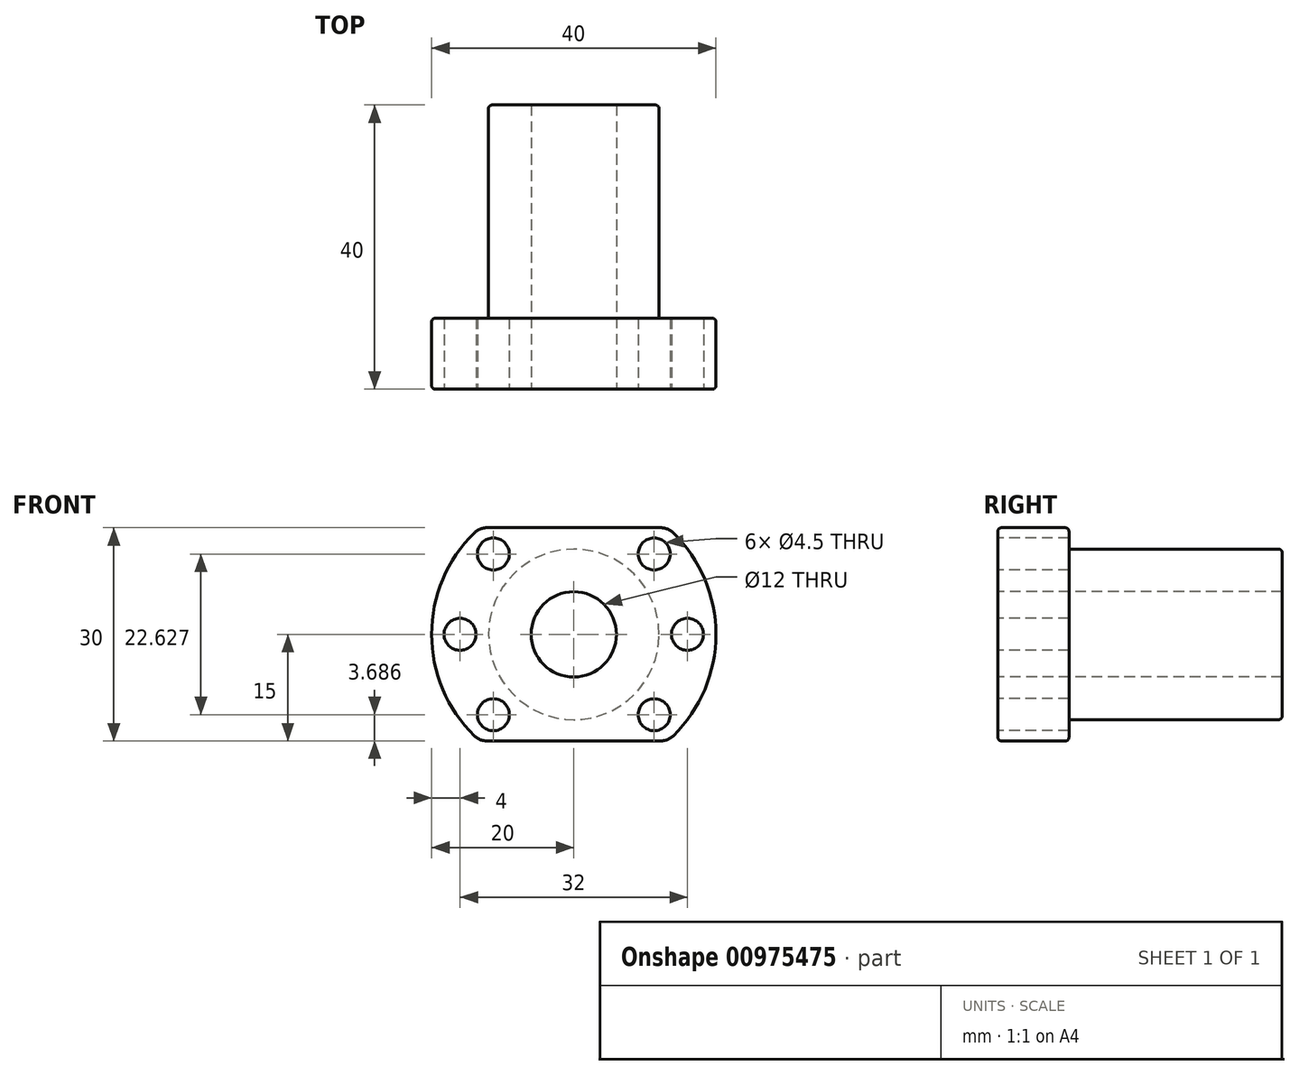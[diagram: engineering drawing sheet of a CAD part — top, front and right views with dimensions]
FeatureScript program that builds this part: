
annotation { "Feature Type Name" : "Feature", "Feature Type Description" : "" }
export const myFeature = defineFeature(function(context is Context, id is Id, definition is map)
    precondition{}
    {
        {
            var Q0;
            Q0=qCreatedBy(makeId("Front.planeOp"),FACE);
            var sketch = newSketch(context, id + "F0", { "sketchPlane" : qUnion([Q0])});
            skCircle(sketch, "E0", {"center": v(0, 0) * mm, "radius": 6 * mm});
            skSolve(sketch);
        }
        {
            var Q0;
            Q0=qCreatedBy(makeId("Front.planeOp"),FACE);
            var sketch = newSketch(context, id + "F1", { "sketchPlane" : qUnion([Q0])});
            skCircle(sketch, "E1.0", {"center": v(0, 0) * mm, "radius": 6 * mm});
            skArc(sketch, "E2", {"start": v(-13.23, 15) * mm, "mid": v(-20, 0) * mm, "end": v(-13.23, -15) * mm});
            skCircle(sketch, "E3", {"center": v(0, 0) * mm, "radius": 12 * mm});
            skLineSegment(sketch, "E4.bottom", {"start": v(-13.23, 15) * mm, "end": v(13.23, 15) * mm});
            skLineSegment(sketch, "E4.top", {"start": v(-13.23, -15) * mm, "end": v(13.23, -15) * mm});
            skArc(sketch, "E5.trimOffspring", {"start": v(13.23, -15) * mm, "mid": v(20, 0) * mm, "end": v(13.23, 15) * mm});
            skCircle(sketch, "E6", {"center": v(0, 0) * mm, "radius": 16 * mm, "construction": true});
            skCircle(sketch, "E7", {"center": v(16, 0) * mm, "radius": 2.25 * mm});
            skCircle(sketch, "E8", {"center": v(11.31, 11.31) * mm, "radius": 2.25 * mm});
            skLineSegment(sketch, "E9", {"start": v(0, 0) * mm, "end": v(11.31, 11.31) * mm, "construction": true});
            skLineSegment(sketch, "E10", {"start": v(0, 0) * mm, "end": v(16, 0) * mm, "construction": true});
            skCircle(sketch, "E11.MirrorC", {"center": v(11.31, -11.31) * mm, "radius": 2.25 * mm});
            skCircle(sketch, "E12.MirrorC", {"center": v(-11.31, 11.31) * mm, "radius": 2.25 * mm});
            skCircle(sketch, "E13.MirrorC", {"center": v(-16, 0) * mm, "radius": 2.25 * mm});
            skCircle(sketch, "E14.MirrorC", {"center": v(-11.31, -11.31) * mm, "radius": 2.25 * mm});
            skSolve(sketch);
        }
        {
            var Q0;
            Q0=makeQuery(id+"F1.imprint","IMPRINT",FACE,{"disambiguationData":[TD([[makeQuery(id+"F1.imprint","IMPRINT",EDGE,{"derivedFrom":sQuery(id+"F1.wireOp",EDGE,"E1.0")}),-1.0]])]});
            extrude(context, id + "F2", {"entities" : qUnion([Q0]), "oppositeDirection" : true, "offsetDistance" : 25 * mm, "depth" : 40 * mm});
        }
        {
            var Q0;
            Q0=makeQuery(id+"F1.imprint","IMPRINT",FACE,{"disambiguationData":[TD([[makeQuery(id+"F1.imprint","IMPRINT",EDGE,{"derivedFrom":sQuery(id+"F1.wireOp",EDGE,"E3")}),-1.0]])]});
            extrude(context, id + "F3", {"entities" : qUnion([Q0]), "operationType" : NewBodyOperationType.ADD, "oppositeDirection" : true, "offsetDistance" : 25 * mm, "depth" : 10 * mm});
        }
        {
            var Q0;
            {var subQ0=sQuery(id+"F1.wireOp",EDGE,"E2");var subQ1=sQuery(id+"F1.wireOp",EDGE,"E4.bottom");Q0=makeQuery(id+"F3.opExtrude","SWEPT_EDGE",EDGE,{"disambiguationData":[OSD([subQ0,subQ1]),TDD([makeQuery(id+"F1.imprint","INTERSECT",VERTEX,{"disambiguationData":[OD(1.0)],"derivedFrom":[subQ0,subQ1]})])]});}
            var Q1;
            {var subQ0=sQuery(id+"F1.wireOp",EDGE,"E2");var subQ1=sQuery(id+"F1.wireOp",EDGE,"E4.bottom");Q1=makeQuery(id+"F3.opExtrude","SWEPT_EDGE",EDGE,{"disambiguationData":[OSD([subQ0,subQ1]),TDD([makeQuery(id+"F1.imprint","INTERSECT",VERTEX,{"disambiguationData":[OD(0.0)],"derivedFrom":[subQ0,subQ1]})])]});}
            var Q2;
            {var subQ0=sQuery(id+"F1.wireOp",EDGE,"E2");var subQ1=sQuery(id+"F1.wireOp",EDGE,"E4.top");Q2=makeQuery(id+"F3.opExtrude","SWEPT_EDGE",EDGE,{"disambiguationData":[OSD([subQ0,subQ1]),TDD([makeQuery(id+"F1.imprint","INTERSECT",VERTEX,{"disambiguationData":[OD(1.0)],"derivedFrom":[subQ0,subQ1]})])]});}
            var Q3;
            {var subQ0=sQuery(id+"F1.wireOp",EDGE,"E2");var subQ1=sQuery(id+"F1.wireOp",EDGE,"E4.top");Q3=makeQuery(id+"F3.opExtrude","SWEPT_EDGE",EDGE,{"disambiguationData":[OSD([subQ0,subQ1]),TDD([makeQuery(id+"F1.imprint","INTERSECT",VERTEX,{"disambiguationData":[OD(0.0)],"derivedFrom":[subQ0,subQ1]})])]});}
            var Q4;
            Q4=makeQuery(id+"F3.opExtrude","SWEPT_EDGE",EDGE,{"disambiguationData":[OSD([sQuery(id+"F1.wireOp",EDGE,"E4.bottom"),sQuery(id+"F1.wireOp",EDGE,"E5.trimOffspring")])]});
            var Q5;
            Q5=makeQuery(id+"F3.opExtrude","SWEPT_EDGE",EDGE,{"disambiguationData":[OSD([sQuery(id+"F1.wireOp",EDGE,"E4.top"),sQuery(id+"F1.wireOp",EDGE,"E5.trimOffspring")])]});
            fillet(context, id + "F4", {"entities" : qUnion([Q0, Q1, Q2, Q3, Q4, Q5]), "radius" : 2.5 * mm, "tangentPropagation" : true, "allowEdgeOverflow" : false});
        }
        {
            var Q0;
            Q0=makeQuery(id+"F3.opExtrude","CAP_EDGE",EDGE,{"disambiguationData":[OSD([sQuery(id+"F1.wireOp",EDGE,"E5.trimOffspring")])],"isStart":false});
            var Q1;
            Q1=makeQuery(id+"F3.opExtrude","CAP_EDGE",EDGE,{"disambiguationData":[OSD([sQuery(id+"F1.wireOp",EDGE,"E5.trimOffspring")])],"isStart":true});
            var Q2;
            Q2=makeQuery(id+"F3.opExtrude","CAP_EDGE",EDGE,{"disambiguationData":[OSD([sQuery(id+"F1.wireOp",EDGE,"E3")])],"isStart":false});
            var Q3;
            Q3=makeQuery(id+"F2.opExtrude","CAP_EDGE",EDGE,{"disambiguationData":[OSD([sQuery(id+"F1.wireOp",EDGE,"E3")])],"isStart":false});
            fillet(context, id + "F5", {"entities" : qUnion([Q0, Q1, Q2, Q3]), "radius" : 0.5 * mm, "tangentPropagation" : true, "allowEdgeOverflow" : false});
        }
    });
